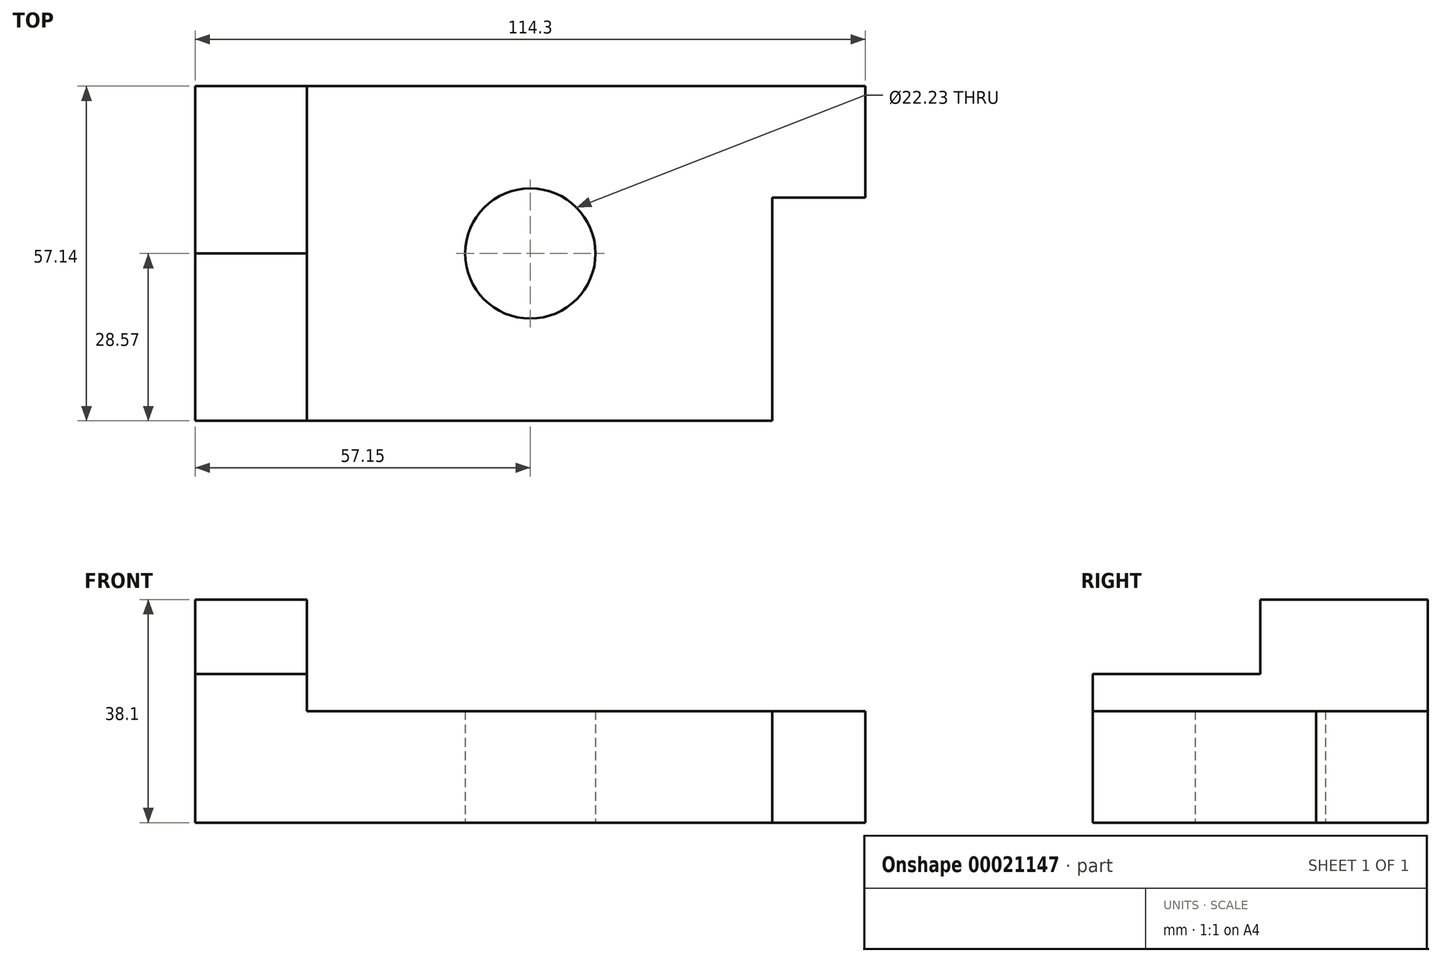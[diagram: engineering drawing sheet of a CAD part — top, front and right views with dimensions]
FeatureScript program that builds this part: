
annotation { "Feature Type Name" : "Feature", "Feature Type Description" : "" }
export const myFeature = defineFeature(function(context is Context, id is Id, definition is map)
    precondition{}
    {
        {
            var Q0;
            Q0=qCreatedBy(makeId("Top.planeOp"),FACE);
            var sketch = newSketch(context, id + "F0", { "sketchPlane" : qUnion([Q0])});
            skLineSegment(sketch, "E0.rect.bottom", {"start": v(-57.15, 28.58) * mm, "end": v(57.15, 28.58) * mm});
            skLineSegment(sketch, "E0.rect.top", {"start": v(-57.15, -28.58) * mm, "end": v(57.15, -28.58) * mm});
            skLineSegment(sketch, "E0.rect.left", {"start": v(-57.15, 28.58) * mm, "end": v(-57.15, -28.58) * mm});
            skLineSegment(sketch, "E0.rect.right", {"start": v(57.15, 28.58) * mm, "end": v(57.15, -28.58) * mm});
            skPoint(sketch, "E0.rect.middle", {"position": v(0, 0) * mm});
            skLineSegment(sketch, "E1.bottom", {"start": v(57.15, -28.58) * mm, "end": v(41.27, -28.58) * mm});
            skLineSegment(sketch, "E1.top", {"start": v(57.15, 9.52) * mm, "end": v(41.27, 9.52) * mm});
            skLineSegment(sketch, "E1.left", {"start": v(57.15, -28.58) * mm, "end": v(57.15, 9.52) * mm});
            skLineSegment(sketch, "E1.right", {"start": v(41.27, -28.58) * mm, "end": v(41.27, 9.52) * mm});
            skCircle(sketch, "E2", {"center": v(0, 0) * mm, "radius": 11.11 * mm});
            skSolve(sketch);
        }
        {
            var Q0;
            Q0=makeQuery(id+"F0.imprint","IMPRINT",FACE,{"disambiguationData":[TD([[makeQuery(id+"F0.imprint","IMPRINT",EDGE,{"derivedFrom":sQuery(id+"F0.wireOp",EDGE,"E0.rect.bottom")}),-1.0]])]});
            extrude(context, id + "F1", {"entities" : qUnion([Q0]), "depth" : 19.05 * mm});
        }
        {
            var Q0;
            Q0=makeQuery(id+"F1.opExtrude","CAP_FACE",FACE,{"disambiguationData":[OSD([sQuery(id+"F0.wireOp",EDGE,"E0.rect.bottom"),sQuery(id+"F0.wireOp",EDGE,"E0.rect.top"),sQuery(id+"F0.wireOp",EDGE,"E0.rect.left"),sQuery(id+"F0.wireOp",EDGE,"E0.rect.right"),sQuery(id+"F0.wireOp",EDGE,"E1.top"),sQuery(id+"F0.wireOp",EDGE,"E1.right"),sQuery(id+"F0.wireOp",EDGE,"E2")])],"isStart":false});
            var sketch = newSketch(context, id + "F2", { "sketchPlane" : qUnion([Q0])});
            skLineSegment(sketch, "E3.bottom", {"start": v(-57.15, 28.58) * mm, "end": v(-38.1, 28.58) * mm});
            skLineSegment(sketch, "E3.top", {"start": v(-57.15, 0) * mm, "end": v(-38.1, 0) * mm});
            skLineSegment(sketch, "E3.left", {"start": v(-57.15, 28.58) * mm, "end": v(-57.15, 0) * mm});
            skLineSegment(sketch, "E3.right", {"start": v(-38.1, 28.58) * mm, "end": v(-38.1, 0) * mm});
            skSolve(sketch);
        }
        {
            var Q0;
            Q0 = qSketchRegion(id + "F2", true);
            extrude(context, id + "F3", {"entities" : qUnion([Q0]), "operationType" : NewBodyOperationType.ADD, "depth" : 19.05 * mm});
        }
        {
            var Q0;
            Q0=makeQuery(id+"F1.opExtrude","CAP_FACE",FACE,{"disambiguationData":[OSD([sQuery(id+"F0.wireOp",EDGE,"E0.rect.bottom"),sQuery(id+"F0.wireOp",EDGE,"E0.rect.top"),sQuery(id+"F0.wireOp",EDGE,"E0.rect.left"),sQuery(id+"F0.wireOp",EDGE,"E0.rect.right"),sQuery(id+"F0.wireOp",EDGE,"E1.top"),sQuery(id+"F0.wireOp",EDGE,"E1.right"),sQuery(id+"F0.wireOp",EDGE,"E2")])],"isStart":false});
            var sketch = newSketch(context, id + "F4", { "sketchPlane" : qUnion([Q0])});
            skLineSegment(sketch, "E4.bottom", {"start": v(-57.15, -28.58) * mm, "end": v(-38.1, -28.58) * mm});
            skLineSegment(sketch, "E4.top", {"start": v(-57.15, 0) * mm, "end": v(-38.1, 0) * mm});
            skLineSegment(sketch, "E4.left", {"start": v(-57.15, -28.58) * mm, "end": v(-57.15, 0) * mm});
            skLineSegment(sketch, "E4.right", {"start": v(-38.1, -28.58) * mm, "end": v(-38.1, 0) * mm});
            skSolve(sketch);
        }
        {
            var Q0;
            Q0 = qSketchRegion(id + "F4", true);
            extrude(context, id + "F5", {"entities" : qUnion([Q0]), "operationType" : NewBodyOperationType.ADD, "depth" : 6.35 * mm});
        }
    });
